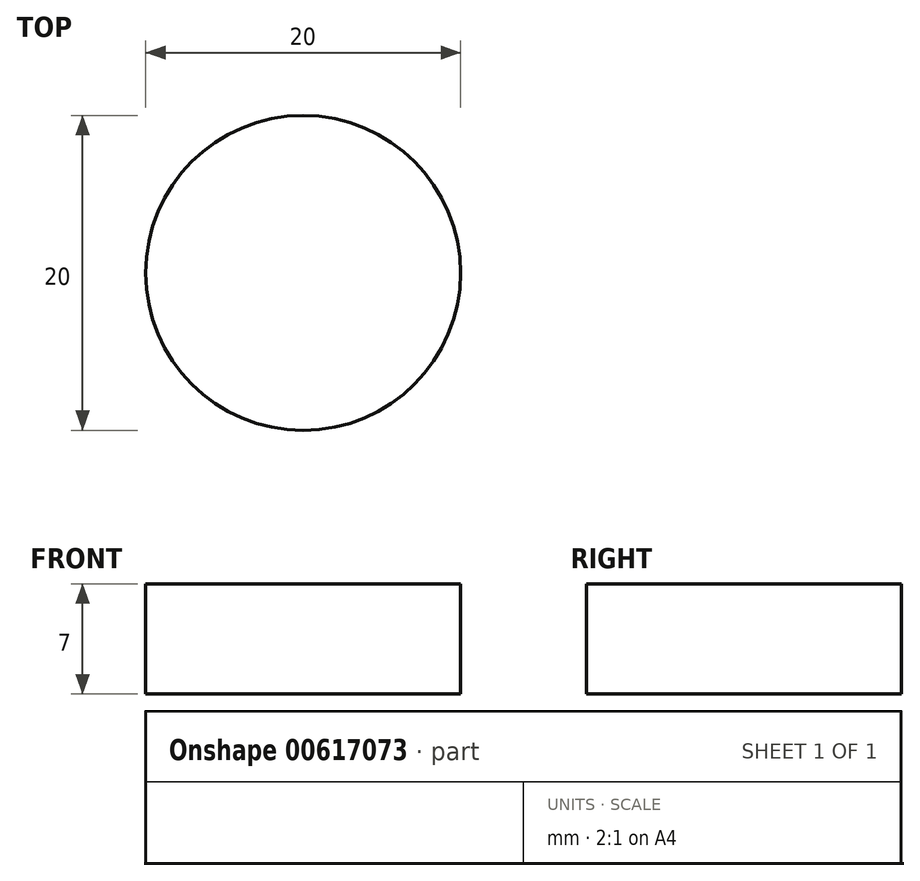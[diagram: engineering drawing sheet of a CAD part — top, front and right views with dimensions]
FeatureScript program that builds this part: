
annotation { "Feature Type Name" : "Feature", "Feature Type Description" : "" }
export const myFeature = defineFeature(function(context is Context, id is Id, definition is map)
    precondition{}
    {
        {
            var Q0;
            Q0=qCreatedBy(makeId("Top.planeOp"),FACE);
            var sketch = newSketch(context, id + "F0", { "sketchPlane" : qUnion([Q0])});
            skCircle(sketch, "E0", {"center": v(0, 0) * mm, "radius": 10 * mm});
            skSolve(sketch);
        }
        {
            var Q0;
            Q0 = qSketchRegion(id + "F0", true);
            extrude(context, id + "F1", {"entities" : qUnion([Q0]), "depth" : 7 * mm, "offsetDistance" : 25 * mm});
        }
    });
